# Revit family: Bike_Rack-Saris_Parking-Vertical_Rack
name_source: partatom
category: Site
revit_build: Autodesk Revit 2014 (Build: 20140709_2115(x64)
units: mm (PartAtom-declared; Revit-internal decimal feet)

## types (8) — shared parameters
3 Parkable Bikes = Yes
Assembly Code = G2040500
Ceiling Clearance = 84 Inches Minimum Ceiling Height
Default Elevation = 48 "
Description = High density bike parking with small footprint
Locking Offset = 0.2 "
Manufacturer = Saris Parking
Mount Color = Paint - Saris Parking - Powder Coat - Shuttle Black
Product Documentation Link = https://www.sarisparking.com
Product Page URL = https://www.sarisparking.com
URL = https://www.sarisparking.com

## per-type parameters (varying)
| type | 4 Parkable Bikes | 6 Parkable Bikes | 8 Parkable Bikes | Bike Track Locking | Depth | Model | Number of Parkable Bikes | Rack Width | Width |
| 3 Bike - Non-Locking | No | No | No | No | 45 " | 8023 | 3 | 50 " | 54 " |
| 4 Bike - Locking | Yes | No | No | Yes | 45 " | 8044 | 4 | 68 " | 74.6 " |
| 6 Bike - Locking | No | Yes | No | Yes | 90 " | 8063 | 6 | 50 " | 54 " |
| 8 Bike - Locking | Yes | Yes | Yes | Yes | 90 " | 8064 | 8 | 68 " | 75 " |
| 3 Bike - Locking | No | No | No | Yes | 45 " | 8043 | 3 | 50 " | 54 " |
| 4 Bike - Non-Locking | Yes | No | No | No | 45 " | 8024 | 4 | 68 " | 74.6 " |
| 6 Bike - Non-Locking | No | Yes | No | No | 90 " | 8033 | 6 | 50 " | 54 " |
| 8 Bike - Non-Locking | Yes | Yes | Yes | No | 90 " | 8034 | 8 | 68 " | 75 " |

## geometry (parser evidence)
native form markers: Sweep x16
no freeform markers — native parametric forms only
